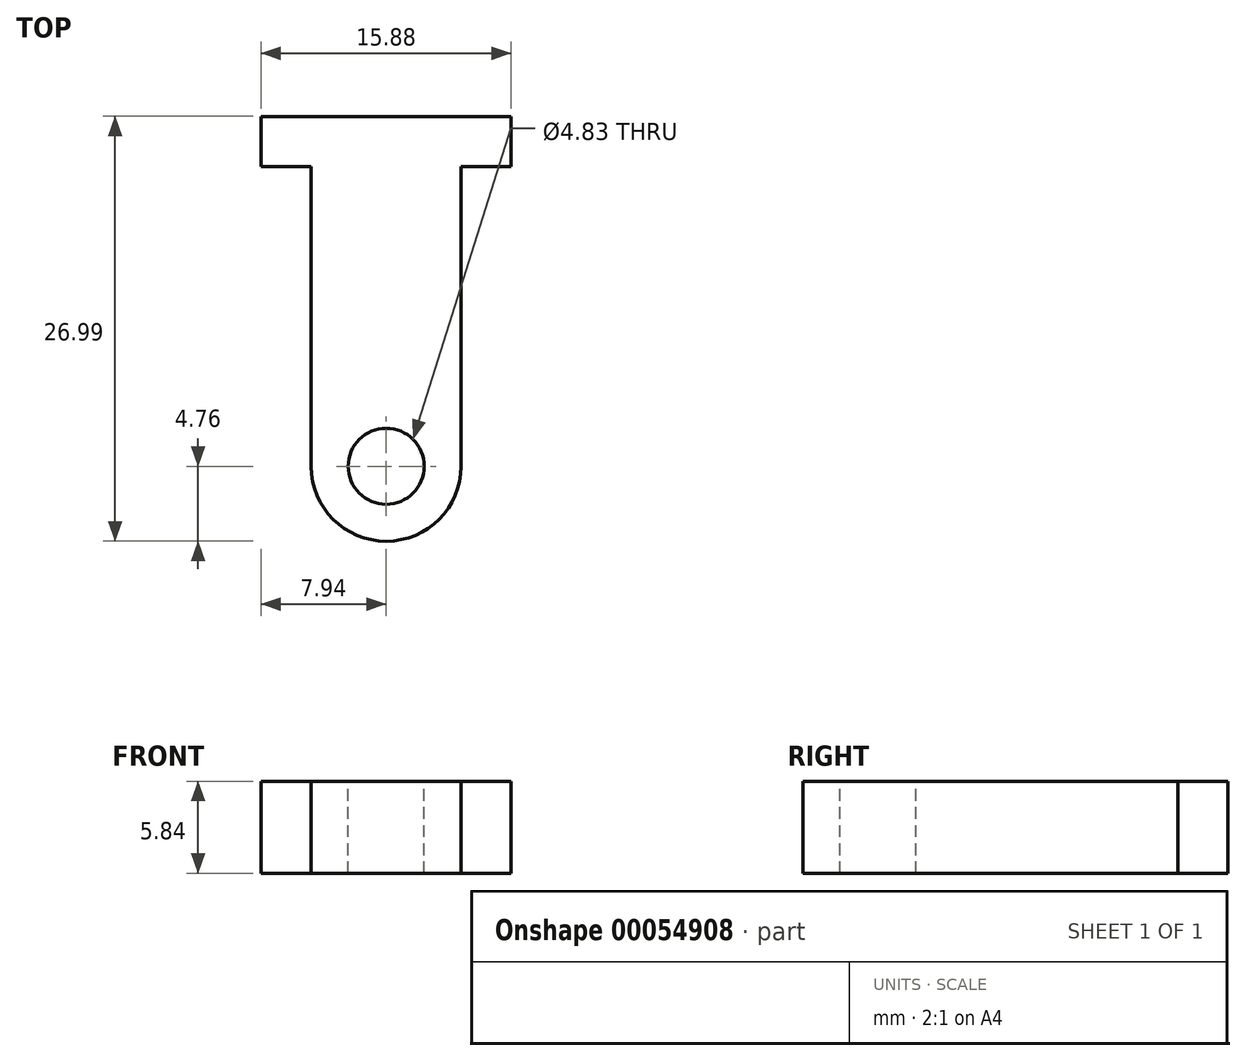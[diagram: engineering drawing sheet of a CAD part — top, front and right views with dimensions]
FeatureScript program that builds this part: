
annotation { "Feature Type Name" : "Feature", "Feature Type Description" : "" }
export const myFeature = defineFeature(function(context is Context, id is Id, definition is map)
    precondition{}
    {
        {
            var Q0;
            Q0=qCreatedBy(makeId("Top.planeOp"),FACE);
            var sketch = newSketch(context, id + "F0", { "sketchPlane" : qUnion([Q0])});
            skCircle(sketch, "E0", {"center": v(0, 0) * mm, "radius": 2.41 * mm});
            skCircle(sketch, "E1", {"center": v(0, 0) * mm, "radius": 4.76 * mm, "construction": true});
            skLineSegment(sketch, "E2", {"start": v(-4.76, 0) * mm, "end": v(-4.76, 19.05) * mm});
            skLineSegment(sketch, "E3", {"start": v(4.76, 0) * mm, "end": v(4.76, 19.05) * mm});
            skLineSegment(sketch, "E4", {"start": v(-4.76, 19.05) * mm, "end": v(-7.94, 19.05) * mm});
            skLineSegment(sketch, "E5", {"start": v(-7.94, 19.05) * mm, "end": v(-7.94, 22.23) * mm});
            skLineSegment(sketch, "E6", {"start": v(-7.94, 22.23) * mm, "end": v(7.94, 22.23) * mm});
            skLineSegment(sketch, "E7", {"start": v(7.94, 22.23) * mm, "end": v(7.94, 19.05) * mm});
            skLineSegment(sketch, "E8", {"start": v(7.94, 19.05) * mm, "end": v(4.76, 19.05) * mm});
            skArc(sketch, "E9", {"start": v(-4.76, 0) * mm, "mid": v(0, -4.76) * mm, "end": v(4.76, 0) * mm});
            skSolve(sketch);
        }
        {
            var Q0;
            Q0=makeQuery(id+"F0.imprint","IMPRINT",FACE,{"disambiguationData":[TD([[makeQuery(id+"F0.imprint","IMPRINT",EDGE,{"derivedFrom":sQuery(id+"F0.wireOp",EDGE,"E0")}),-1.0]])]});
            extrude(context, id + "F1", {"entities" : qUnion([Q0]), "oppositeDirection" : true, "depth" : 5.84 * mm});
        }
    });
